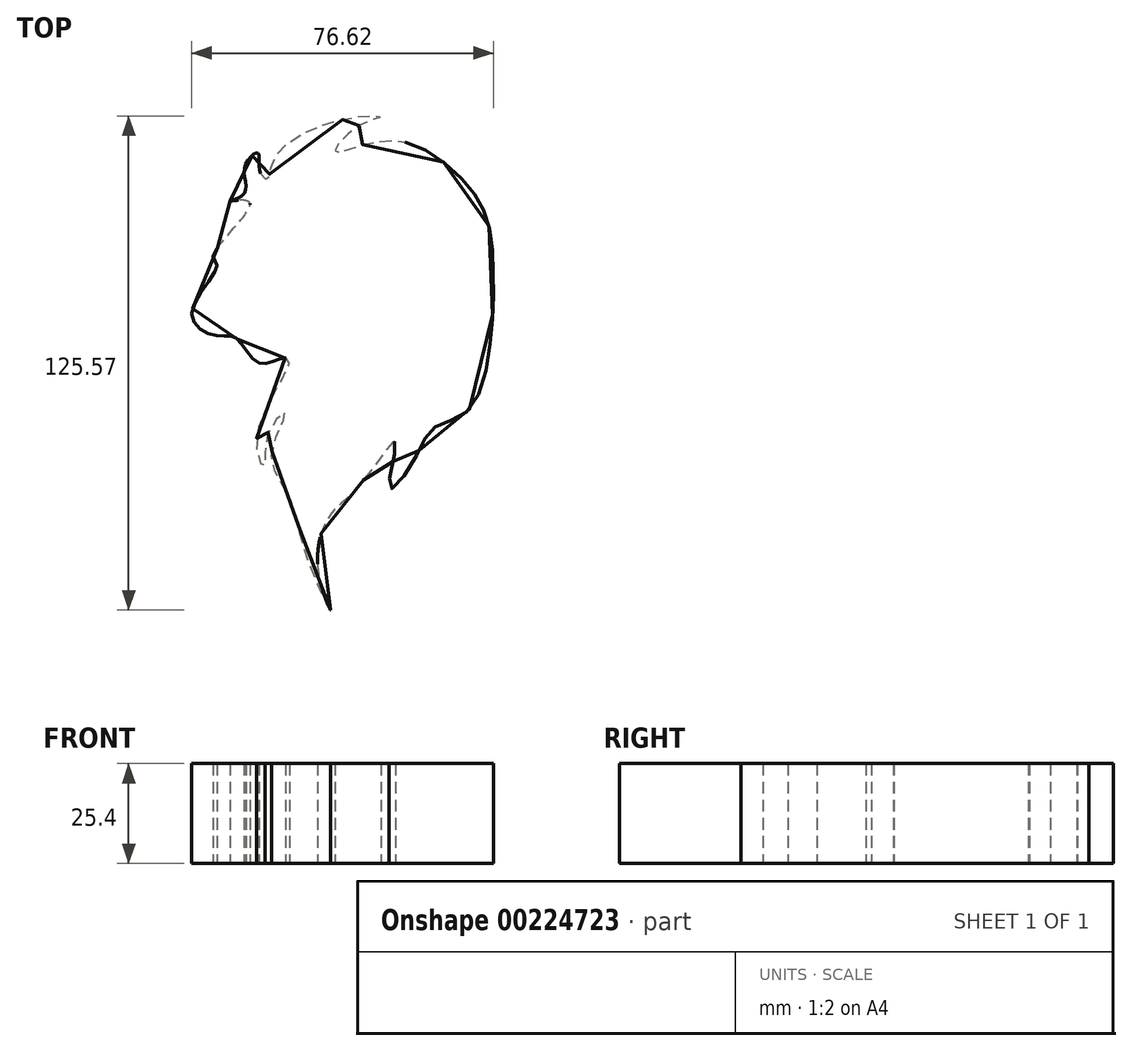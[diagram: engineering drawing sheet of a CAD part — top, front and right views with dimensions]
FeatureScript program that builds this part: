
annotation { "Feature Type Name" : "Feature", "Feature Type Description" : "" }
export const myFeature = defineFeature(function(context is Context, id is Id, definition is map)
    precondition{}
    {
        {
            var Q0;
            Q0=qCreatedBy(makeId("Top.planeOp"),FACE);
            var sketch = newSketch(context, id + "F0", { "sketchPlane" : qUnion([Q0])});
            skLineSegment(sketch, "E0.bottom", {"start": v(-42.85, 66.23) * mm, "end": v(39.54, 66.23) * mm});
            skLineSegment(sketch, "E0.top", {"start": v(-42.85, -66.76) * mm, "end": v(39.54, -66.76) * mm});
            skLineSegment(sketch, "E0.left", {"start": v(-42.85, 66.23) * mm, "end": v(-42.85, -66.76) * mm});
            skLineSegment(sketch, "E0.right", {"start": v(39.54, 66.23) * mm, "end": v(39.54, -66.76) * mm});
            skFitSpline(sketch, "E1", {"points": [v(-4.35, -60.96) * mm, v(-9.94, -48.54) * mm, v(-15.11, -31.57) * mm, v(-19.25, -21.22) * mm, v(-15.73, -10.87) * mm, v(-20.29, -16.25) * mm, v(-21.12, -24.53) * mm, v(-22.98, -16.66) * mm, v(-14.7, 2.38) * mm, v(-17.18, 2.8) * mm, v(-22.77, 1.97) * mm, v(-28.36, 8.18) * mm, v(-33.54, 8.8) * mm, v(-39.54, 14.39) * mm, v(-33.12, 26.6) * mm, v(-34.16, 29.09) * mm, v(-24.84, 42.54) * mm, v(-29.8, 42.95) * mm, v(-26.3, 44.82) * mm, v(-26.08, 51.65) * mm, v(-22.77, 55.17) * mm, v(-22.36, 50.82) * mm, v(-20.29, 48.54) * mm, v(-18.22, 54.55) * mm, v(1.86, 64.28) * mm, v(8.49, 64.28) * mm, v(3.1, 62.2) * mm, v(-3.1, 55.58) * mm, v(3.1, 57.03) * mm, v(16.56, 57.45) * mm, v(29.4, 48.13) * mm, v(35.4, 38.6) * mm, v(37.06, 24.12) * mm, v(36.23, 6.52) * mm, v(30.43, -10.45) * mm, v(21.94, -14.6) * mm, v(16.77, -23.08) * mm, v(10.76, -29.91) * mm, v(12.21, -18.32) * mm, v(8.28, -22.46) * mm, v(0, -32.4) * mm, v(-5.18, -37.99) * mm, v(-7.25, -52.27) * mm, v(-4.35, -60.96) * mm]});
            skSolve(sketch);
        }
        {
            var Q0;
            Q0=makeQuery(id+"F0.imprint","IMPRINT",FACE,{"disambiguationData":[TD([[makeQuery(id+"F0.imprint","IMPRINT",EDGE,{"derivedFrom":sQuery(id+"F0.wireOp",EDGE,"E1")}),-1.0]])]});
            extrude(context, id + "F1", {"entities" : qUnion([Q0]), "depth" : 25.4 * mm});
        }
    });
